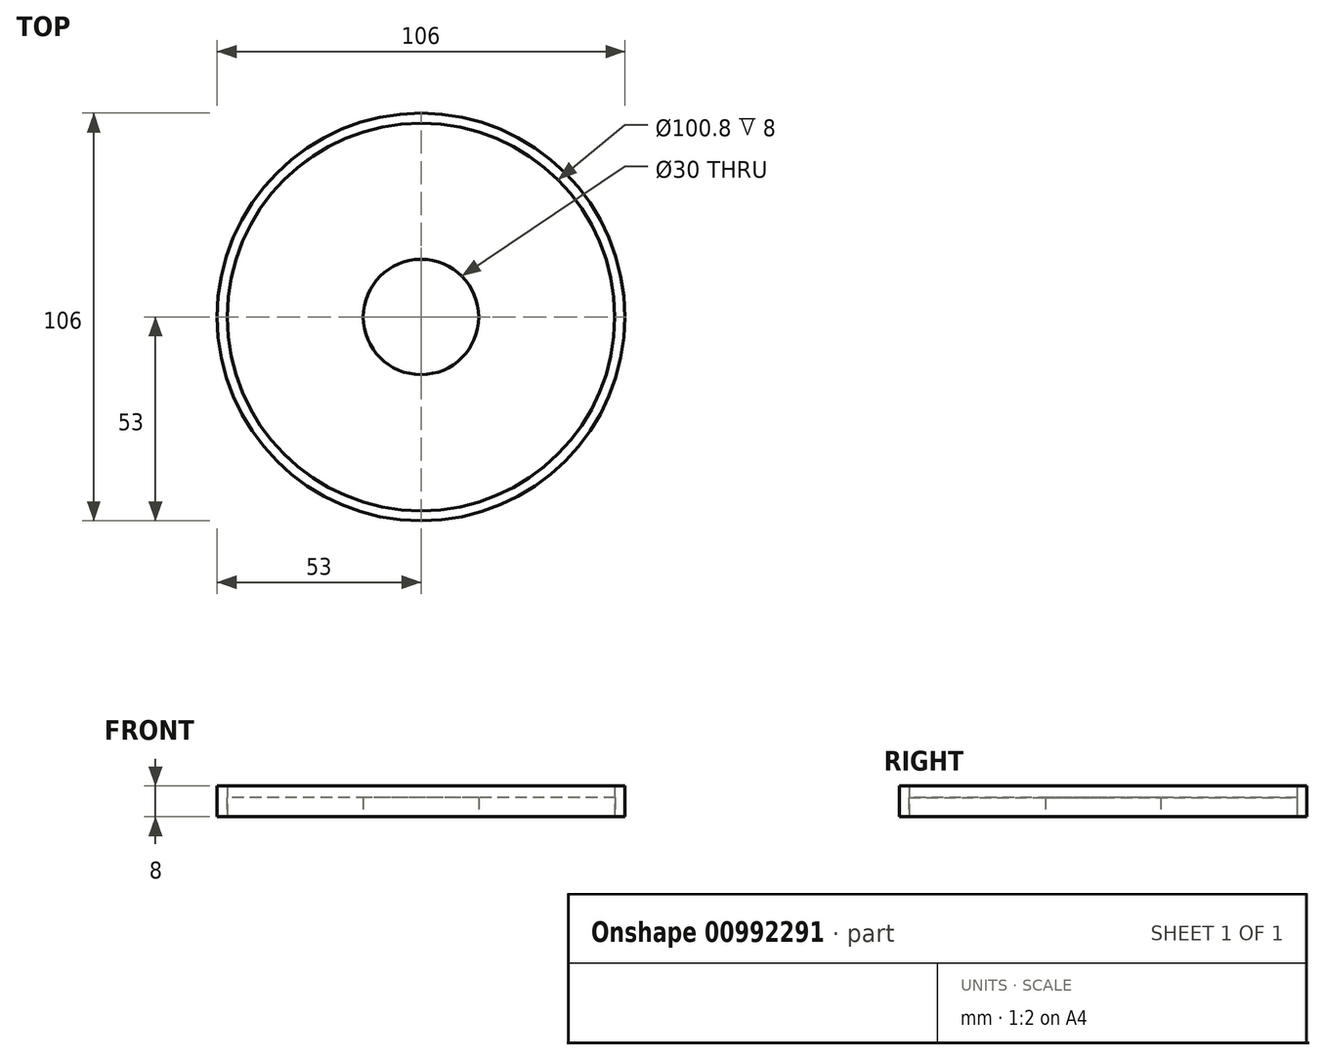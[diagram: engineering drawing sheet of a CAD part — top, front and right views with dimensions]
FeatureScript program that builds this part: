
annotation { "Feature Type Name" : "Feature", "Feature Type Description" : "" }
export const myFeature = defineFeature(function(context is Context, id is Id, definition is map)
    precondition{}
    {
        {
            var Q0;
            Q0=qCreatedBy(makeId("Top.planeOp"),FACE);
            var sketch = newSketch(context, id + "F0", { "sketchPlane" : qUnion([Q0])});
            skCircle(sketch, "E0", {"center": v(0, 0) * mm, "radius": 50.5 * mm});
            skCircle(sketch, "E1", {"center": v(0, 0) * mm, "radius": 15 * mm});
            skSolve(sketch);
        }
        {
            var Q0;
            Q0=qSketchRegion(id+"F0",true);
            extrude(context, id + "F1", {"entities" : qUnion([Q0]), "depth" : 5 * mm, "offsetDistance" : 25 * mm});
        }
        {
            var Q0;
            Q0=qCreatedBy(makeId("Top.planeOp"),FACE);
            var sketch = newSketch(context, id + "F2", { "sketchPlane" : qUnion([Q0])});
            skCircle(sketch, "E2", {"center": v(0, 0) * mm, "radius": 53 * mm});
            skCircle(sketch, "E3", {"center": v(0, 0) * mm, "radius": 50.4 * mm});
            skSolve(sketch);
        }
        {
            var Q0;
            Q0=makeQuery(id+"F2.imprint","IMPRINT",FACE,{"disambiguationData":[TD([[makeQuery(id+"F2.imprint","IMPRINT",EDGE,{"derivedFrom":sQuery(id+"F2.wireOp",EDGE,"E2")}),1.0]])]});
            var Q1;
            Q1=sQuery(id+"F2.wireOp",EDGE,"E2");
            var Q2;
            Q2=sQuery(id+"F2.wireOp",EDGE,"E3");
            extrude(context, id + "F3", {"entities" : qUnion([Q0]), "surfaceOperationType" : NewSurfaceOperationType.ADD, "surfaceEntities" : qUnion([Q1, Q2]), "depth" : 8 * mm, "offsetDistance" : 25 * mm});
        }
    });
